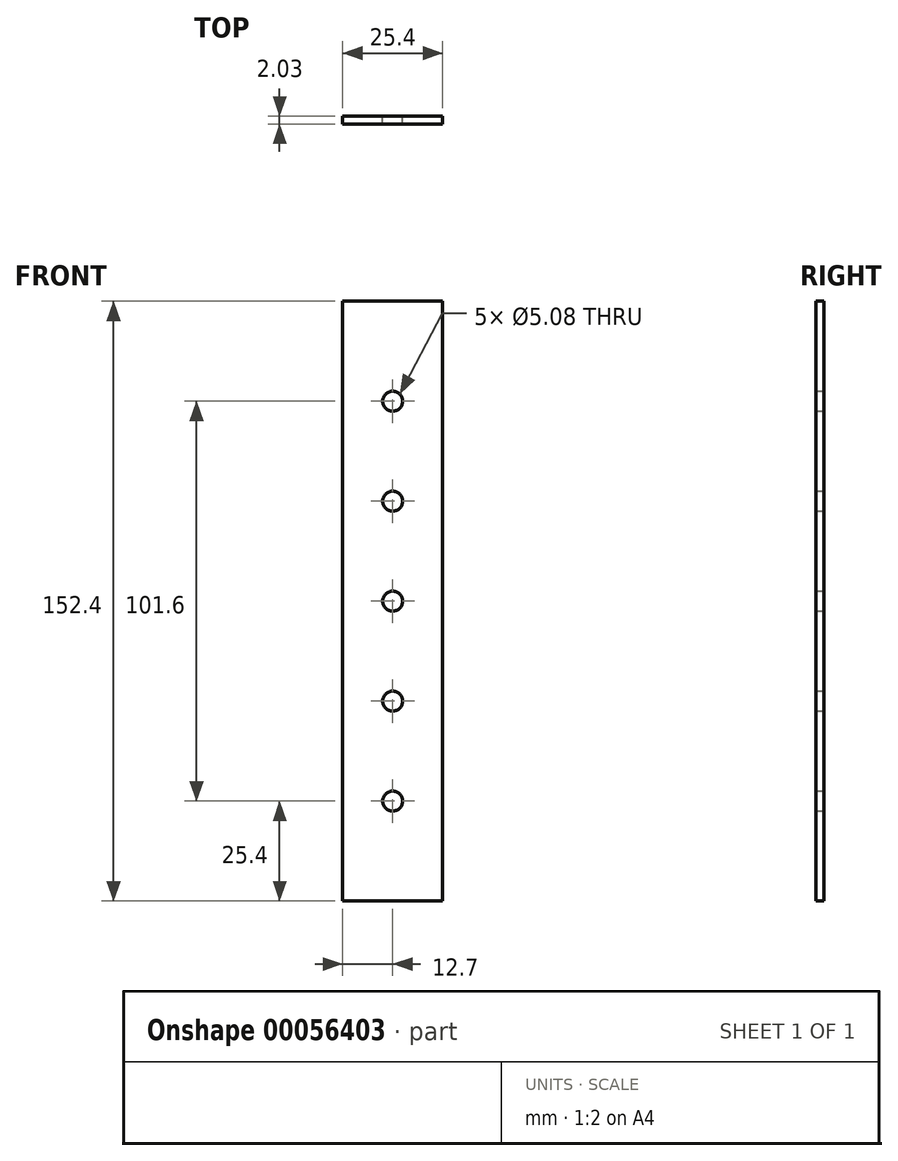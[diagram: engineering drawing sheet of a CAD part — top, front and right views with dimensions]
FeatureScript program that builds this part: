
annotation { "Feature Type Name" : "Feature", "Feature Type Description" : "" }
export const myFeature = defineFeature(function(context is Context, id is Id, definition is map)
    precondition{}
    {
        {
            var Q0;
            Q0=qCreatedBy(makeId("Front.planeOp"),FACE);
            var sketch = newSketch(context, id + "F0", { "sketchPlane" : qUnion([Q0])});
            skLineSegment(sketch, "E0.bottom", {"start": v(0, 0) * mm, "end": v(25.4, 0) * mm});
            skLineSegment(sketch, "E0.top", {"start": v(0, 152.4) * mm, "end": v(25.4, 152.4) * mm});
            skLineSegment(sketch, "E0.left", {"start": v(0, 0) * mm, "end": v(0, 152.4) * mm});
            skLineSegment(sketch, "E0.right", {"start": v(25.4, 0) * mm, "end": v(25.4, 152.4) * mm});
            skLineSegment(sketch, "E1.bottom", {"start": v(12.7, 152.4) * mm, "end": v(12.7, 152.4) * mm});
            skLineSegment(sketch, "E1.top", {"start": v(12.7, 0) * mm, "end": v(12.7, 0) * mm});
            skLineSegment(sketch, "E2.bottom", {"start": v(0, 152.4) * mm, "end": v(0, 152.4) * mm});
            skLineSegment(sketch, "E2.top", {"start": v(0, 127) * mm, "end": v(0, 127) * mm});
            skLineSegment(sketch, "E2.left", {"start": v(0, 152.4) * mm, "end": v(0, 127) * mm, "construction": true});
            skLineSegment(sketch, "E2.right", {"start": v(0, 152.4) * mm, "end": v(0, 127) * mm, "construction": true});
            skLineSegment(sketch, "E3.top", {"start": v(0, 101.6) * mm, "end": v(0, 101.6) * mm});
            skLineSegment(sketch, "E3.left", {"start": v(0, 127) * mm, "end": v(0, 101.6) * mm, "construction": true});
            skLineSegment(sketch, "E3.right", {"start": v(0, 127) * mm, "end": v(0, 101.6) * mm, "construction": true});
            skLineSegment(sketch, "E4", {"start": v(0, 101.6) * mm, "end": v(0, 76.2) * mm, "construction": true});
            skLineSegment(sketch, "E5", {"start": v(0, 76.2) * mm, "end": v(0, 50.8) * mm, "construction": true});
            skLineSegment(sketch, "E6", {"start": v(0, 50.8) * mm, "end": v(0, 25.4) * mm, "construction": true});
            skPoint(sketch, "E7", {"position": v(12.7, 127) * mm});
            skPoint(sketch, "E8", {"position": v(12.7, 101.6) * mm});
            skPoint(sketch, "E9", {"position": v(12.7, 76.2) * mm});
            skPoint(sketch, "E10", {"position": v(12.7, 50.8) * mm});
            skPoint(sketch, "E11", {"position": v(12.7, 25.4) * mm});
            skLineSegment(sketch, "E12.trimOffspring", {"start": v(12.7, 132.08) * mm, "end": v(12.7, 132.08) * mm, "construction": true});
            skCircle(sketch, "E13", {"center": v(12.7, 127) * mm, "radius": 2.54 * mm});
            skPoint(sketch, "E14.rect.right.start.orphan", {"position": v(10.16, 106.68) * mm});
            skPoint(sketch, "E14.rect.left.start.orphan", {"position": v(15.24, 106.68) * mm});
            skPoint(sketch, "E15.trimOffspring.end.orphan", {"position": v(15.24, 96.52) * mm});
            skPoint(sketch, "E15.trimOffspring.start.orphan", {"position": v(10.16, 96.52) * mm});
            skCircle(sketch, "E16", {"center": v(12.7, 101.6) * mm, "radius": 2.54 * mm});
            skPoint(sketch, "E17.rect.right.start.orphan", {"position": v(10.16, 81.28) * mm});
            skPoint(sketch, "E17.rect.left.start.orphan", {"position": v(15.24, 81.28) * mm});
            skPoint(sketch, "E18.end.orphan", {"position": v(15.24, 71.12) * mm});
            skPoint(sketch, "E18.start.orphan", {"position": v(10.16, 71.12) * mm});
            skCircle(sketch, "E19", {"center": v(12.7, 76.2) * mm, "radius": 2.54 * mm});
            skPoint(sketch, "E20.rect.right.start.orphan", {"position": v(10.16, 55.88) * mm});
            skPoint(sketch, "E20.rect.left.start.orphan", {"position": v(15.24, 55.88) * mm});
            skPoint(sketch, "E21.trimOffspring.end.orphan", {"position": v(15.24, 45.72) * mm});
            skPoint(sketch, "E21.trimOffspring.start.orphan", {"position": v(10.16, 45.72) * mm});
            skCircle(sketch, "E22", {"center": v(12.7, 50.8) * mm, "radius": 2.54 * mm});
            skPoint(sketch, "E23.rect.left.start.orphan", {"position": v(15.24, 30.48) * mm});
            skPoint(sketch, "E23.rect.right.start.orphan", {"position": v(10.16, 30.48) * mm});
            skPoint(sketch, "E24.trimOffspring.end.orphan", {"position": v(15.24, 20.32) * mm});
            skPoint(sketch, "E24.trimOffspring.start.orphan", {"position": v(10.16, 20.32) * mm});
            skCircle(sketch, "E25", {"center": v(12.7, 25.4) * mm, "radius": 2.54 * mm});
            skSolve(sketch);
        }
        {
            var Q0;
            Q0=qSketchRegion(id+"F0",true);
            extrude(context, id + "F1", {"entities" : qUnion([Q0]), "depth" : 2.03 * mm});
        }
    });
